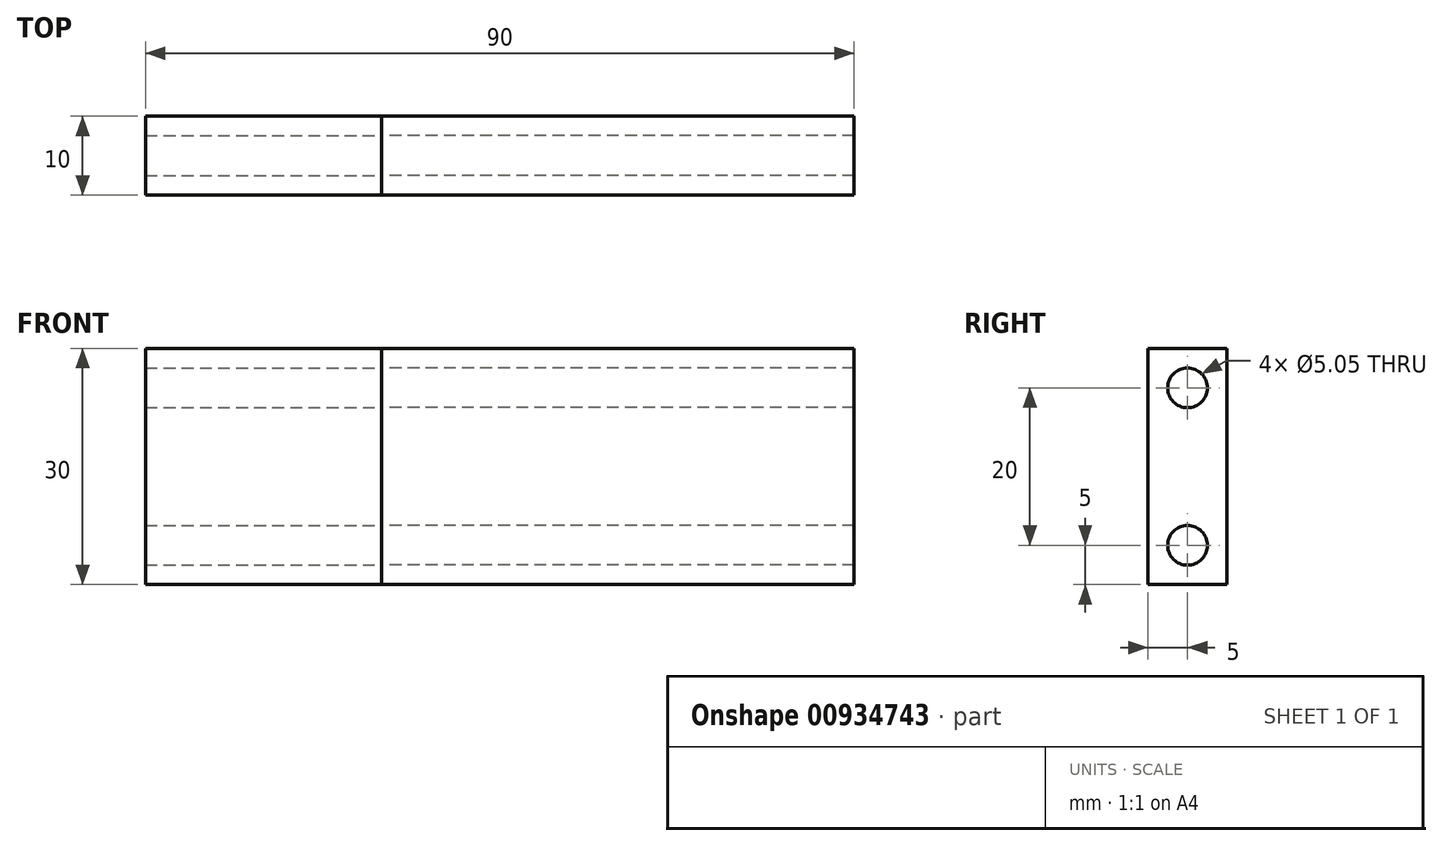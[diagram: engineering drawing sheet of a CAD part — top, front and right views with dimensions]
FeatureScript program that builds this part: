
annotation { "Feature Type Name" : "Feature", "Feature Type Description" : "" }
export const myFeature = defineFeature(function(context is Context, id is Id, definition is map)
    precondition{}
    {
        {
            var Q0;
            Q0=qCreatedBy(makeId("Right.planeOp"),FACE);
            var sketch = newSketch(context, id + "F0", { "sketchPlane" : qUnion([Q0])});
            skLineSegment(sketch, "E0.bottom", {"start": v(5, 15) * mm, "end": v(-5, 15) * mm});
            skLineSegment(sketch, "E0.top", {"start": v(5, -15) * mm, "end": v(-5, -15) * mm});
            skLineSegment(sketch, "E0.left", {"start": v(5, 15) * mm, "end": v(5, -15) * mm});
            skLineSegment(sketch, "E0.right", {"start": v(-5, 15) * mm, "end": v(-5, -15) * mm});
            skPoint(sketch, "E0.middle", {"position": v(0, 0) * mm});
            skLineSegment(sketch, "E1", {"start": v(0, 0) * mm, "end": v(0, 10) * mm, "construction": true});
            skLineSegment(sketch, "E2", {"start": v(0, 0) * mm, "end": v(0, -10) * mm, "construction": true});
            skCircle(sketch, "E3", {"center": v(0, -10) * mm, "radius": 2.52 * mm});
            skCircle(sketch, "E4", {"center": v(0, 10) * mm, "radius": 2.52 * mm});
            skSolve(sketch);
        }
        {
            var Q0;
            Q0 = qSketchRegion(id + "F0", true);
            extrude(context, id + "F1", {"entities" : qUnion([Q0]), "depth" : 60 * mm, "offsetDistance" : 25 * mm});
        }
        {
            var Q0;
            Q0=qCreatedBy(makeId("Right.planeOp"),FACE);
            var sketch = newSketch(context, id + "F2", { "sketchPlane" : qUnion([Q0])});
            skLineSegment(sketch, "E5.bottom", {"start": v(5, 15) * mm, "end": v(-5, 15) * mm});
            skLineSegment(sketch, "E5.top", {"start": v(5, -15) * mm, "end": v(-5, -15) * mm});
            skLineSegment(sketch, "E5.left", {"start": v(5, 15) * mm, "end": v(5, -15) * mm});
            skLineSegment(sketch, "E5.right", {"start": v(-5, 15) * mm, "end": v(-5, -15) * mm});
            skPoint(sketch, "E5.middle", {"position": v(0, 0) * mm});
            skLineSegment(sketch, "E6", {"start": v(0, 0) * mm, "end": v(0, 10) * mm, "construction": true});
            skLineSegment(sketch, "E7", {"start": v(0, 0) * mm, "end": v(0, -10) * mm, "construction": true});
            skCircle(sketch, "E8", {"center": v(0, -10) * mm, "radius": 2.52 * mm});
            skCircle(sketch, "E9", {"center": v(0, 10) * mm, "radius": 2.52 * mm});
            skSolve(sketch);
        }
        {
            var Q0;
            Q0 = qSketchRegion(id + "F2", true);
            extrude(context, id + "F3", {"entities" : qUnion([Q0]), "oppositeDirection" : true, "depth" : 30 * mm, "offsetDistance" : 25 * mm});
        }
    });
